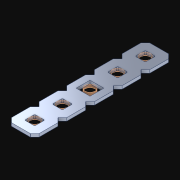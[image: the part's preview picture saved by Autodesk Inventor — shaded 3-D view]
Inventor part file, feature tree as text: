
AUTODESK INVENTOR PART (.ipt)
format: ipt  version: 2021 (Build 250183000, 183)  size: 177,152 bytes
history: native  units: in
note: dims shown in document units (in); Inventor stores cm internally (conversion verified against a paired STEP export)
features: other x6, extrude x5, pattern_linear x1, sketch x1
ambient origin geometry x8: Origin, YZ Plane, XZ Plane, XY Plane, X Axis, Y Axis, Z Axis, Center Point
bodies: Solid1 (feature_tree)
feature tree (13):
  pattern_linear  "Rectangular Pattern1"  Spacing1=1.0in  [1 undecoded]
  sketch  "Sketch1"  dims[d0=0.182in d1=1.0in d2=0.0in d3=1.9685in d5=0.5in]
  other  "Srf1"
  other  "Srf2"
  other  "Srf3"
  other  "Srf4"
  other  "Srf5"
  parser-record x1  (decoder bookkeeping rows leaked as tree rows — omitted from the tree; the rows remain in map.json)
  extrude  "ExtrusionSrf1"  Depth=0.5in
  extrude  "ExtrusionSrf2"  [1 undecoded]
  extrude  "ExtrusionSrf3"  [1 undecoded]
  extrude  "ExtrusionSrf4"  [1 undecoded]
  extrude  "ExtrusionSrf5"  [1 undecoded]
note: 5 required parameter values undecoded (feature->parameter linkage not recoverable at this tier; creation-order binding heuristic only, values carry confidence <= 0.55)
